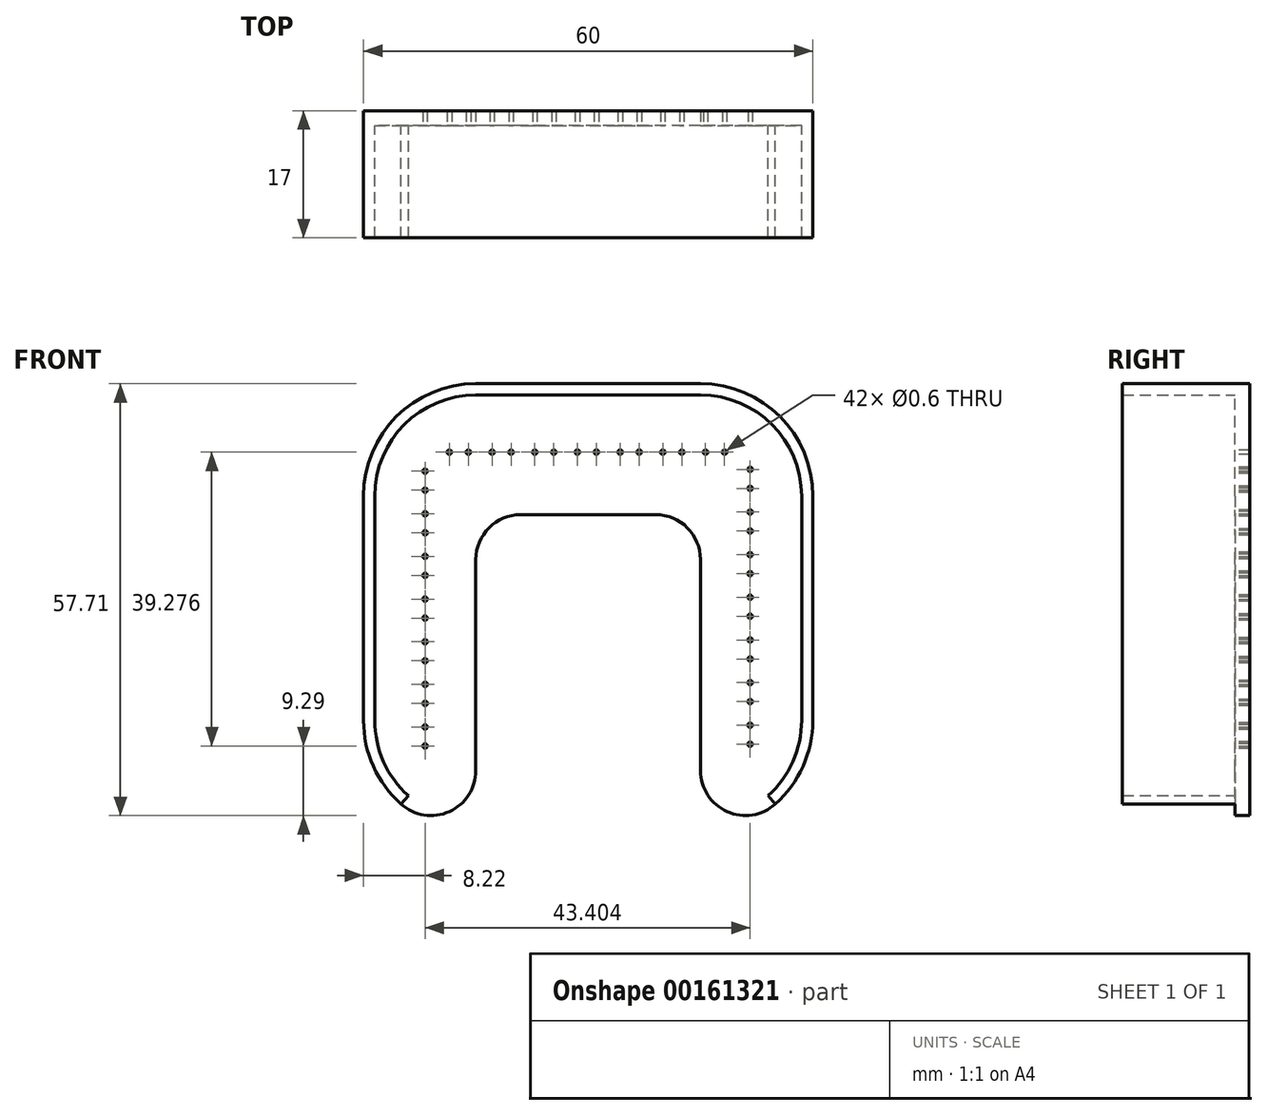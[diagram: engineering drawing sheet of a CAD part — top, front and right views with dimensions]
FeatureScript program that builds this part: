
annotation { "Feature Type Name" : "Feature", "Feature Type Description" : "" }
export const myFeature = defineFeature(function(context is Context, id is Id, definition is map)
    precondition{}
    {
        {
            var Q0;
            Q0=qCreatedBy(makeId("Front.planeOp"),FACE);
            var sketch = newSketch(context, id + "F0", { "sketchPlane" : qUnion([Q0])});
            skCircle(sketch, "E0", {"center": v(-21.78, 18.32) * mm, "radius": 0.3 * mm});
            skCircle(sketch, "E1", {"center": v(-21.78, 15.78) * mm, "radius": 0.3 * mm});
            skCircle(sketch, "E2", {"center": v(-21.78, 12.62) * mm, "radius": 0.3 * mm});
            skCircle(sketch, "E3", {"center": v(-21.78, 10.08) * mm, "radius": 0.3 * mm});
            skCircle(sketch, "E4", {"center": v(-21.78, 6.92) * mm, "radius": 0.3 * mm});
            skCircle(sketch, "E5", {"center": v(-21.78, 4.38) * mm, "radius": 0.3 * mm});
            skCircle(sketch, "E6", {"center": v(-21.78, 1.22) * mm, "radius": 0.3 * mm});
            skCircle(sketch, "E7", {"center": v(-21.78, -1.32) * mm, "radius": 0.3 * mm});
            skCircle(sketch, "E8", {"center": v(-21.78, -4.48) * mm, "radius": 0.3 * mm});
            skCircle(sketch, "E9", {"center": v(-21.78, -7.02) * mm, "radius": 0.3 * mm});
            skCircle(sketch, "E10", {"center": v(-21.78, -10.18) * mm, "radius": 0.3 * mm});
            skCircle(sketch, "E11", {"center": v(-21.78, -12.72) * mm, "radius": 0.3 * mm});
            skCircle(sketch, "E12", {"center": v(-21.78, -15.88) * mm, "radius": 0.3 * mm});
            skCircle(sketch, "E13", {"center": v(-21.78, -18.42) * mm, "radius": 0.3 * mm});
            skCircle(sketch, "E14", {"center": v(21.62, 18.56) * mm, "radius": 0.3 * mm});
            skCircle(sketch, "E15", {"center": v(21.62, 16.02) * mm, "radius": 0.3 * mm});
            skCircle(sketch, "E16", {"center": v(21.62, 12.86) * mm, "radius": 0.3 * mm});
            skCircle(sketch, "E17", {"center": v(21.62, 10.32) * mm, "radius": 0.3 * mm});
            skCircle(sketch, "E18", {"center": v(21.62, 7.16) * mm, "radius": 0.3 * mm});
            skCircle(sketch, "E19", {"center": v(21.62, 4.62) * mm, "radius": 0.3 * mm});
            skCircle(sketch, "E20", {"center": v(21.62, 1.46) * mm, "radius": 0.3 * mm});
            skCircle(sketch, "E21", {"center": v(21.62, -1.08) * mm, "radius": 0.3 * mm});
            skCircle(sketch, "E22", {"center": v(21.62, -4.24) * mm, "radius": 0.3 * mm});
            skCircle(sketch, "E23", {"center": v(21.62, -6.78) * mm, "radius": 0.3 * mm});
            skCircle(sketch, "E24", {"center": v(21.62, -9.94) * mm, "radius": 0.3 * mm});
            skCircle(sketch, "E25", {"center": v(21.62, -12.48) * mm, "radius": 0.3 * mm});
            skCircle(sketch, "E26", {"center": v(21.62, -15.64) * mm, "radius": 0.3 * mm});
            skCircle(sketch, "E27", {"center": v(21.62, -18.18) * mm, "radius": 0.3 * mm});
            skCircle(sketch, "E28", {"center": v(-18.53, 20.86) * mm, "radius": 0.3 * mm});
            skCircle(sketch, "E29", {"center": v(-16, 20.86) * mm, "radius": 0.3 * mm});
            skCircle(sketch, "E30", {"center": v(-12.83, 20.86) * mm, "radius": 0.3 * mm});
            skCircle(sketch, "E31", {"center": v(-10.3, 20.86) * mm, "radius": 0.3 * mm});
            skCircle(sketch, "E32", {"center": v(-7.13, 20.86) * mm, "radius": 0.3 * mm});
            skCircle(sketch, "E33", {"center": v(-4.6, 20.86) * mm, "radius": 0.3 * mm});
            skCircle(sketch, "E34", {"center": v(-1.43, 20.86) * mm, "radius": 0.3 * mm});
            skCircle(sketch, "E35", {"center": v(1.1, 20.86) * mm, "radius": 0.3 * mm});
            skCircle(sketch, "E36", {"center": v(4.27, 20.86) * mm, "radius": 0.3 * mm});
            skCircle(sketch, "E37", {"center": v(6.8, 20.86) * mm, "radius": 0.3 * mm});
            skCircle(sketch, "E38", {"center": v(9.97, 20.86) * mm, "radius": 0.3 * mm});
            skCircle(sketch, "E39", {"center": v(12.5, 20.86) * mm, "radius": 0.3 * mm});
            skCircle(sketch, "E40", {"center": v(15.67, 20.86) * mm, "radius": 0.3 * mm});
            skCircle(sketch, "E41", {"center": v(18.2, 20.86) * mm, "radius": 0.3 * mm});
            skPoint(sketch, "E42.middle", {"position": v(0, 0) * mm});
            skSolve(sketch);
        }
        {
            var Q0;
            Q0=qCreatedBy(makeId("Front.planeOp"),FACE);
            var sketch = newSketch(context, id + "F1", { "sketchPlane" : qUnion([Q0])});
            skLineSegment(sketch, "E43.bottom", {"start": v(30, 30) * mm, "end": v(-30, 30) * mm});
            skLineSegment(sketch, "E43.top", {"start": v(30, -30) * mm, "end": v(-30, -30) * mm});
            skLineSegment(sketch, "E43.left", {"start": v(30, 30) * mm, "end": v(30, -30) * mm});
            skLineSegment(sketch, "E43.right", {"start": v(-30, 30) * mm, "end": v(-30, -30) * mm});
            skPoint(sketch, "E43.middle", {"position": v(0, 0) * mm});
            skSolve(sketch);
        }
        {
            var Q0;
            Q0 = qSketchRegion(id + "F1", true);
            extrude(context, id + "F2", {"entities" : qUnion([Q0]), "oppositeDirection" : true, "depth" : 2 * mm});
        }
        {
            var Q0;
            Q0 = qSketchRegion(id + "F0", true);
            extrude(context, id + "F3", {"entities" : qUnion([Q0]), "operationType" : NewBodyOperationType.REMOVE, "oppositeDirection" : true, "depth" : 2 * mm});
        }
        {
            var Q0;
            Q0=makeQuery(id+"F2.opExtrude","SWEPT_EDGE",EDGE,{"disambiguationData":[OSD([sQuery(id+"F1.wireOp",EDGE,"E43.bottom"),sQuery(id+"F1.wireOp",EDGE,"E43.right")])]});
            var Q1;
            Q1=makeQuery(id+"F2.opExtrude","SWEPT_EDGE",EDGE,{"disambiguationData":[OSD([sQuery(id+"F1.wireOp",EDGE,"E43.bottom"),sQuery(id+"F1.wireOp",EDGE,"E43.left")])]});
            var Q2;
            Q2=makeQuery(id+"F2.opExtrude","SWEPT_EDGE",EDGE,{"disambiguationData":[OSD([sQuery(id+"F1.wireOp",EDGE,"E43.top"),sQuery(id+"F1.wireOp",EDGE,"E43.left")])]});
            var Q3;
            Q3=makeQuery(id+"F2.opExtrude","SWEPT_EDGE",EDGE,{"disambiguationData":[OSD([sQuery(id+"F1.wireOp",EDGE,"E43.top"),sQuery(id+"F1.wireOp",EDGE,"E43.right")])]});
            fillet(context, id + "F4", {"entities" : qUnion([Q0, Q1, Q2, Q3]), "radius" : 15 * mm, "tangentPropagation" : true, "allowEdgeOverflow" : false});
        }
        {
            var Q0;
            Q0=makeQuery(id+"F2.opExtrude","CAP_FACE",FACE,{"disambiguationData":[OSD([sQuery(id+"F1.wireOp",EDGE,"E43.bottom"),sQuery(id+"F1.wireOp",EDGE,"E43.top"),sQuery(id+"F1.wireOp",EDGE,"E43.left"),sQuery(id+"F1.wireOp",EDGE,"E43.right")])],"isStart":true});
            var sketch = newSketch(context, id + "F5", { "sketchPlane" : qUnion([Q0])});
            skLineSegment(sketch, "E44.bottom", {"start": v(-15, -30) * mm, "end": v(15, -30) * mm});
            skLineSegment(sketch, "E44.top", {"start": v(-15, 12.5) * mm, "end": v(15, 12.5) * mm});
            skLineSegment(sketch, "E44.left", {"start": v(-15, -30) * mm, "end": v(-15, 12.5) * mm});
            skLineSegment(sketch, "E44.right", {"start": v(15, -30) * mm, "end": v(15, 12.5) * mm});
            skSolve(sketch);
        }
        {
            var Q0;
            Q0 = qSketchRegion(id + "F5", true);
            extrude(context, id + "F6", {"entities" : qUnion([Q0]), "operationType" : NewBodyOperationType.REMOVE, "oppositeDirection" : true, "depth" : 2 * mm});
        }
        {
            var Q0;
            {var subQ0=sQuery(id+"F1.wireOp",EDGE,"E43.left");var subQ1=sQuery(id+"F1.wireOp",EDGE,"E43.top");Q0=makeQuery(id+"F6.boolean.opBoolean","MERGE",EDGE,{"derivedFrom":[makeQuery(id+"F4.opFillet","BLEND_EDGE",EDGE,{"blendedFrom":[makeQuery(id+"F2.opExtrude","SWEPT_EDGE",EDGE,{"disambiguationData":[OSD([subQ1,subQ0])]}),makeQuery(id+"F2.opExtrude","SWEPT_FACE",FACE,{"disambiguationData":[OSD([subQ1])]})],"blendedInto":[makeQuery(id+"F2.opExtrude","SWEPT_FACE",FACE,{"disambiguationData":[OSD([subQ1])]})]}),makeQuery(id+"F6.opExtrude","SWEPT_EDGE",EDGE,{"disambiguationData":[OSD([sQuery(id+"F1.wireOp",EDGE,"E43.bottom"),subQ1,subQ0,sQuery(id+"F1.wireOp",EDGE,"E43.right"),sQuery(id+"F5.wireOp",EDGE,"E44.bottom"),sQuery(id+"F5.wireOp",EDGE,"E44.right")])]})]});}
            var Q1;
            {var subQ0=sQuery(id+"F1.wireOp",EDGE,"E43.right");var subQ1=sQuery(id+"F1.wireOp",EDGE,"E43.top");Q1=makeQuery(id+"F6.boolean.opBoolean","MERGE",EDGE,{"derivedFrom":[makeQuery(id+"F4.opFillet","BLEND_EDGE",EDGE,{"blendedFrom":[makeQuery(id+"F2.opExtrude","SWEPT_EDGE",EDGE,{"disambiguationData":[OSD([subQ1,subQ0])]}),makeQuery(id+"F2.opExtrude","SWEPT_FACE",FACE,{"disambiguationData":[OSD([subQ1])]})],"blendedInto":[makeQuery(id+"F2.opExtrude","SWEPT_FACE",FACE,{"disambiguationData":[OSD([subQ1])]})]}),makeQuery(id+"F6.opExtrude","SWEPT_EDGE",EDGE,{"disambiguationData":[OSD([sQuery(id+"F1.wireOp",EDGE,"E43.bottom"),subQ1,sQuery(id+"F1.wireOp",EDGE,"E43.left"),subQ0,sQuery(id+"F5.wireOp",EDGE,"E44.bottom"),sQuery(id+"F5.wireOp",EDGE,"E44.left")])]})]});}
            var Q2;
            Q2=makeQuery(id+"F6.boolean.opBoolean","COPY",EDGE,{"derivedFrom":makeQuery(id+"F6.opExtrude","SWEPT_EDGE",EDGE,{"disambiguationData":[OSD([sQuery(id+"F5.wireOp",EDGE,"E44.top"),sQuery(id+"F5.wireOp",EDGE,"E44.left")])]})});
            var Q3;
            Q3=makeQuery(id+"F6.boolean.opBoolean","COPY",EDGE,{"derivedFrom":makeQuery(id+"F6.opExtrude","SWEPT_EDGE",EDGE,{"disambiguationData":[OSD([sQuery(id+"F5.wireOp",EDGE,"E44.top"),sQuery(id+"F5.wireOp",EDGE,"E44.right")])]})});
            fillet(context, id + "F7", {"entities" : qUnion([Q0, Q1, Q2, Q3]), "radius" : 6 * mm, "tangentPropagation" : true, "allowEdgeOverflow" : false});
        }
        {
            var Q0;
            Q0=makeQuery(id+"F2.opExtrude","CAP_FACE",FACE,{"disambiguationData":[OSD([sQuery(id+"F1.wireOp",EDGE,"E43.bottom"),sQuery(id+"F1.wireOp",EDGE,"E43.top"),sQuery(id+"F1.wireOp",EDGE,"E43.left"),sQuery(id+"F1.wireOp",EDGE,"E43.right")])],"isStart":true});
            var sketch = newSketch(context, id + "F8", { "sketchPlane" : qUnion([Q0])});
            skArc(sketch, "E45.0", {"start": v(-28.5, -15) * mm, "mid": v(-27.32, -20.51) * mm, "end": v(-24, -25.06) * mm});
            skLineSegment(sketch, "E45.1", {"start": v(-28.5, 15) * mm, "end": v(-28.5, -15) * mm});
            skArc(sketch, "E45.2", {"start": v(-15, 28.5) * mm, "mid": v(-24.55, 24.55) * mm, "end": v(-28.5, 15) * mm});
            skArc(sketch, "E45.3", {"start": v(24, -25.06) * mm, "mid": v(27.32, -20.51) * mm, "end": v(28.5, -15) * mm});
            skLineSegment(sketch, "E45.4", {"start": v(28.5, 15) * mm, "end": v(28.5, -15) * mm});
            skArc(sketch, "E45.5", {"start": v(28.5, 15) * mm, "mid": v(24.55, 24.55) * mm, "end": v(15, 28.5) * mm});
            skLineSegment(sketch, "E45.6", {"start": v(15, 28.5) * mm, "end": v(-15, 28.5) * mm});
            skLineSegment(sketch, "E46", {"start": v(-24, -25.06) * mm, "end": v(-25, -26.18) * mm});
            skLineSegment(sketch, "E47", {"start": v(25, -26.18) * mm, "end": v(24, -25.06) * mm});
            skSolve(sketch);
        }
        {
            var Q0;
            Q0 = qSketchRegion(id + "F8", true);
            var Q1;
            Q1=makeQuery(id+"F8.imprint","IMPRINT",FACE,{"disambiguationData":[TD([[makeQuery(id+"F8.imprint","IMPRINT",EDGE,{"derivedFrom":sQuery(id+"F8.wireOp",EDGE,"E45.0")}),-1.0]])]});
            extrude(context, id + "F9", {"entities" : qUnion([Q0, Q1]), "operationType" : NewBodyOperationType.ADD, "depth" : 15 * mm});
        }
    });
